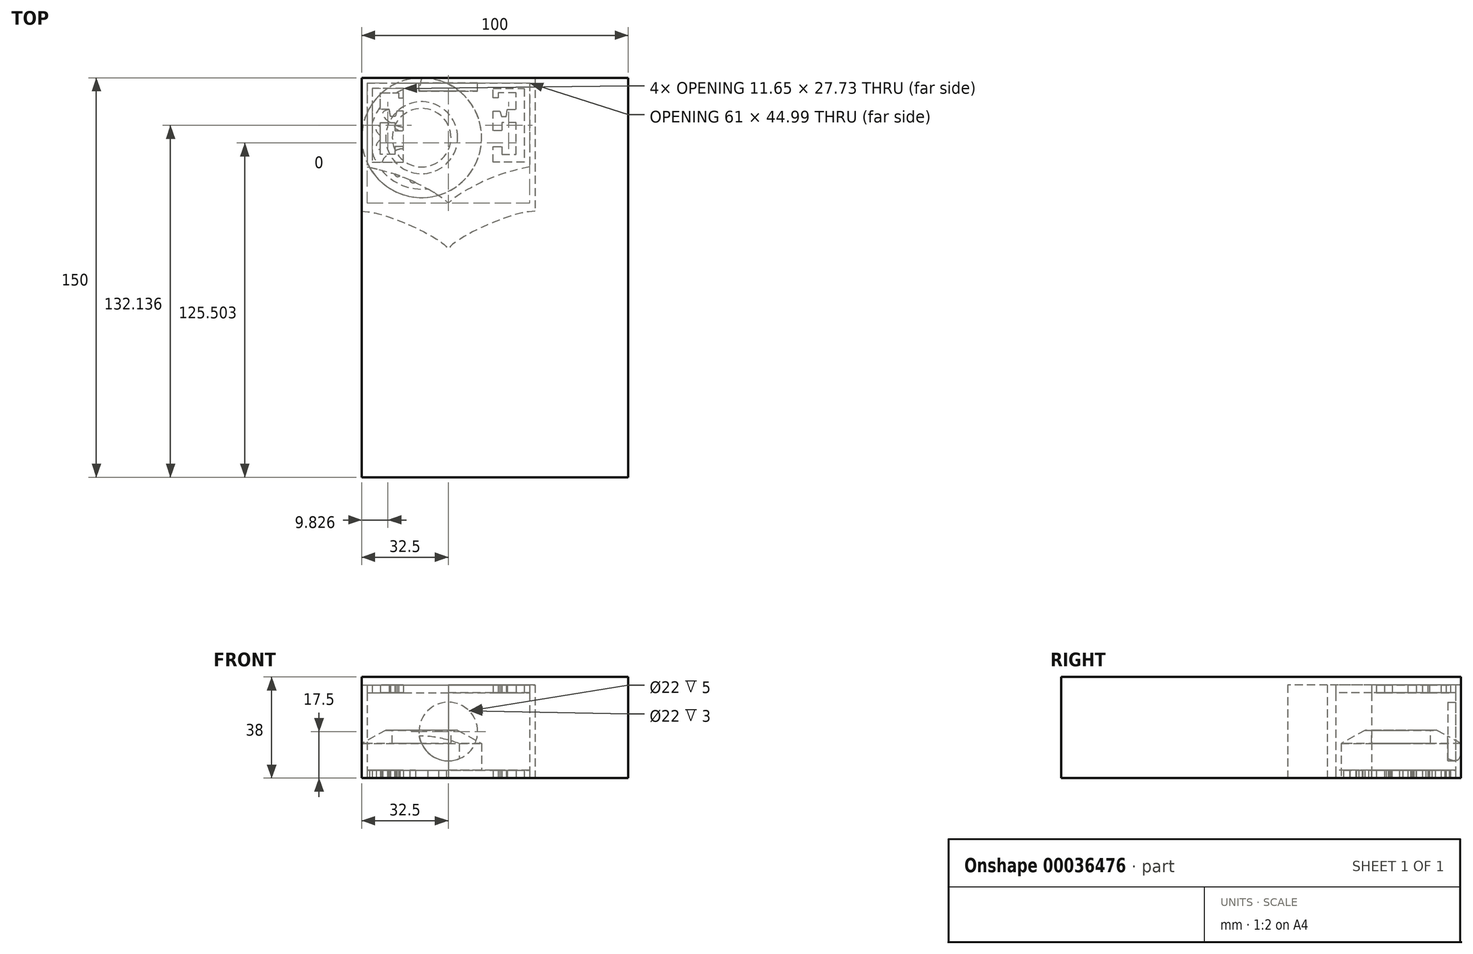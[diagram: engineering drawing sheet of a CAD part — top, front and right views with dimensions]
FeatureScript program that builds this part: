
annotation { "Feature Type Name" : "Feature", "Feature Type Description" : "" }
export const myFeature = defineFeature(function(context is Context, id is Id, definition is map)
    precondition{}
    {
        {
            var Q0;
            Q0=qCreatedBy(makeId("Top.planeOp"),FACE);
            var sketch = newSketch(context, id + "F0", { "sketchPlane" : qUnion([Q0])});
            skSolve(sketch);
        }
        {
            var Q0;
            Q0=qCreatedBy(makeId("Top.planeOp"),FACE);
            var sketch = newSketch(context, id + "F1", { "sketchPlane" : qUnion([Q0])});
            skLineSegment(sketch, "E0.0", {"start": v(0, 0) * mm, "end": v(0, -65) * mm, "construction": true});
            skLineSegment(sketch, "E1.0", {"start": v(65, 0) * mm, "end": v(0, 0) * mm, "construction": true});
            skLineSegment(sketch, "E2.0", {"start": v(0, -65) * mm, "end": v(65, -65) * mm, "construction": true});
            skLineSegment(sketch, "E3", {"start": v(32.5, 0) * mm, "end": v(32.5, -65) * mm, "construction": true});
            skLineSegment(sketch, "E4", {"start": v(32.5, 0) * mm, "end": v(0, 0) * mm});
            skLineSegment(sketch, "E5", {"start": v(0, 0) * mm, "end": v(0, -50.15) * mm});
            skFitSpline(sketch, "E6", {"points": [v(0, -50.15) * mm, v(3.66, -50.5) * mm, v(10.36, -52.32) * mm, v(21.46, -56.9) * mm, v(28.51, -60.84) * mm, v(31.27, -62.9) * mm, v(32.5, -65) * mm], "startDerivative": vector(25.8, -1.39) * mm, "endDerivative": vector(0, -17.33) * mm});
            skLineSegment(sketch, "E7.1", {"start": v(2, -2) * mm, "end": v(2, -33.52) * mm});
            skLineSegment(sketch, "E7.2", {"start": v(32.5, -2) * mm, "end": v(2, -2) * mm});
            skLineSegment(sketch, "E8", {"start": v(13.81, -7.5) * mm, "end": v(15.65, -7.5) * mm});
            skLineSegment(sketch, "E9", {"start": v(15.65, -7.5) * mm, "end": v(15.65, -4) * mm});
            skLineSegment(sketch, "E10", {"start": v(15.65, -4) * mm, "end": v(4, -4) * mm});
            skLineSegment(sketch, "E11", {"start": v(4, -4) * mm, "end": v(4, -31.73) * mm});
            skLineSegment(sketch, "E12", {"start": v(4, -31.73) * mm, "end": v(15.65, -31.73) * mm});
            skLineSegment(sketch, "E13", {"start": v(15.65, -31.73) * mm, "end": v(15.65, -25.83) * mm});
            skLineSegment(sketch, "E14", {"start": v(15.65, -25.83) * mm, "end": v(12.43, -25.83) * mm});
            skLineSegment(sketch, "E15", {"start": v(12.43, -25.83) * mm, "end": v(12.43, -28.7) * mm});
            skLineSegment(sketch, "E16", {"start": v(12.43, -28.7) * mm, "end": v(7.02, -28.7) * mm});
            skLineSegment(sketch, "E17", {"start": v(7.02, -28.7) * mm, "end": v(7.02, -16.77) * mm});
            skLineSegment(sketch, "E18", {"start": v(7.02, -16.77) * mm, "end": v(12.43, -16.77) * mm});
            skLineSegment(sketch, "E19", {"start": v(12.43, -16.77) * mm, "end": v(12.43, -19.9) * mm});
            skLineSegment(sketch, "E20", {"start": v(12.43, -19.9) * mm, "end": v(15.65, -19.9) * mm});
            skLineSegment(sketch, "E21", {"start": v(15.65, -19.9) * mm, "end": v(15.65, -12.5) * mm});
            skLineSegment(sketch, "E22", {"start": v(15.65, -12.5) * mm, "end": v(13.18, -12.5) * mm});
            skLineSegment(sketch, "E23", {"start": v(13.18, -12.5) * mm, "end": v(12.54, -14.54) * mm});
            skLineSegment(sketch, "E24", {"start": v(12.54, -14.54) * mm, "end": v(10.76, -14.54) * mm});
            skLineSegment(sketch, "E25", {"start": v(10.76, -14.54) * mm, "end": v(10.36, -11.89) * mm});
            skLineSegment(sketch, "E26", {"start": v(10.36, -11.89) * mm, "end": v(7.02, -11.89) * mm});
            skLineSegment(sketch, "E27", {"start": v(7.02, -11.89) * mm, "end": v(7.02, -5.62) * mm});
            skLineSegment(sketch, "E28", {"start": v(7.02, -5.62) * mm, "end": v(13.81, -5.62) * mm});
            skLineSegment(sketch, "E29", {"start": v(13.81, -5.62) * mm, "end": v(13.81, -7.5) * mm});
            skFitSpline(sketch, "E30", {"points": [v(32.5, -14.07) * mm, v(31.31, -16.82) * mm, v(29.03, -19.54) * mm, v(27.59, -20.35) * mm, v(25.23, -20.31) * mm, v(24.13, -19.17) * mm, v(24.1, -17.02) * mm, v(26.54, -15) * mm, v(26.34, -12.46) * mm, v(23.52, -11.92) * mm, v(21.24, -12.62) * mm, v(21.17, -14.07) * mm, v(21.2, -24.54) * mm, v(23.35, -27) * mm, v(26.61, -27.06) * mm, v(28.6, -27.9) * mm, v(30.64, -30.18) * mm, v(32.5, -32.97) * mm], "startDerivative": vector(-15.31, -45.36) * mm, "endDerivative": vector(28.23, -44.45) * mm});
            skLineSegment(sketch, "E31", {"start": v(32.5, -32.97) * mm, "end": v(32.5, -14.07) * mm});
            skLineSegment(sketch, "E32", {"start": v(32.5, -65) * mm, "end": v(32.5, -64.37) * mm});
            skLineSegment(sketch, "E33.MirrorCS", {"start": v(32.5, 0) * mm, "end": v(65, 0) * mm});
            skLineSegment(sketch, "E34.MirrorCS", {"start": v(32.5, -2) * mm, "end": v(63, -2) * mm});
            skLineSegment(sketch, "E35.MirrorCS", {"start": v(63, -2) * mm, "end": v(63, -33.52) * mm});
            skLineSegment(sketch, "E36.MirrorCS", {"start": v(65, 0) * mm, "end": v(65, -50.15) * mm});
            skFitSpline(sketch, "E37.MirrorCS", {"points": [v(65, -50.15) * mm, v(61.34, -50.5) * mm, v(54.64, -52.32) * mm, v(43.54, -56.9) * mm, v(36.49, -60.84) * mm, v(33.73, -62.9) * mm, v(32.5, -65) * mm], "startDerivative": vector(-25.8, -1.39) * mm, "endDerivative": vector(0, -17.33) * mm});
            skLineSegment(sketch, "E38.MirrorCS", {"start": v(49.35, -4) * mm, "end": v(61, -4) * mm});
            skLineSegment(sketch, "E39.MirrorCS", {"start": v(49.35, -7.5) * mm, "end": v(49.35, -4) * mm});
            skLineSegment(sketch, "E40.MirrorCS", {"start": v(57.98, -5.62) * mm, "end": v(51.19, -5.62) * mm});
            skLineSegment(sketch, "E41.MirrorCS", {"start": v(51.19, -5.62) * mm, "end": v(51.19, -7.5) * mm});
            skFitSpline(sketch, "E42.MirrorCS", {"points": [v(32.5, -14.07) * mm, v(33.69, -16.82) * mm, v(35.97, -19.54) * mm, v(37.41, -20.35) * mm, v(39.77, -20.31) * mm, v(40.87, -19.17) * mm, v(40.9, -17.02) * mm, v(38.46, -15) * mm, v(38.66, -12.46) * mm, v(41.48, -11.92) * mm, v(43.76, -12.62) * mm, v(43.83, -14.07) * mm, v(43.8, -24.54) * mm, v(41.65, -27) * mm, v(38.39, -27.06) * mm, v(36.4, -27.9) * mm, v(34.36, -30.18) * mm, v(32.5, -32.97) * mm], "startDerivative": vector(15.31, -45.36) * mm, "endDerivative": vector(-28.23, -44.45) * mm});
            skLineSegment(sketch, "E43.MirrorCS", {"start": v(49.35, -25.83) * mm, "end": v(52.57, -25.83) * mm});
            skLineSegment(sketch, "E44.MirrorCS", {"start": v(49.35, -31.73) * mm, "end": v(49.35, -25.83) * mm});
            skLineSegment(sketch, "E45.MirrorCS", {"start": v(52.57, -25.83) * mm, "end": v(52.57, -28.7) * mm});
            skLineSegment(sketch, "E46.MirrorCS", {"start": v(52.57, -28.7) * mm, "end": v(57.98, -28.7) * mm});
            skLineSegment(sketch, "E47.MirrorCS", {"start": v(61, -31.73) * mm, "end": v(49.35, -31.73) * mm});
            skLineSegment(sketch, "E48.MirrorCS", {"start": v(61, -4) * mm, "end": v(61, -31.73) * mm});
            skLineSegment(sketch, "E49.MirrorCS", {"start": v(57.98, -16.77) * mm, "end": v(52.57, -16.77) * mm});
            skLineSegment(sketch, "E50.MirrorCS", {"start": v(52.57, -16.77) * mm, "end": v(52.57, -19.9) * mm});
            skLineSegment(sketch, "E51.MirrorCS", {"start": v(52.57, -19.9) * mm, "end": v(49.35, -19.9) * mm});
            skLineSegment(sketch, "E52.MirrorCS", {"start": v(49.35, -19.9) * mm, "end": v(49.35, -12.5) * mm});
            skLineSegment(sketch, "E53.MirrorCS", {"start": v(49.35, -12.5) * mm, "end": v(51.82, -12.5) * mm});
            skLineSegment(sketch, "E54.MirrorCS", {"start": v(51.82, -12.5) * mm, "end": v(52.46, -14.54) * mm});
            skLineSegment(sketch, "E55.MirrorCS", {"start": v(52.46, -14.54) * mm, "end": v(54.24, -14.54) * mm});
            skLineSegment(sketch, "E56.MirrorCS", {"start": v(54.24, -14.54) * mm, "end": v(54.64, -11.89) * mm});
            skLineSegment(sketch, "E57.MirrorCS", {"start": v(54.64, -11.89) * mm, "end": v(57.98, -11.89) * mm});
            skLineSegment(sketch, "E58.MirrorCS", {"start": v(57.98, -11.89) * mm, "end": v(57.98, -5.62) * mm});
            skLineSegment(sketch, "E59.MirrorCS", {"start": v(51.19, -7.5) * mm, "end": v(49.35, -7.5) * mm});
            skLineSegment(sketch, "E60.MirrorCS", {"start": v(57.98, -28.7) * mm, "end": v(57.98, -16.77) * mm});
            skFitSpline(sketch, "E61", {"points": [v(2, -33.52) * mm, v(6.2, -34.35) * mm, v(11.5, -35.88) * mm, v(18.02, -38.31) * mm, v(23.08, -40.78) * mm, v(28.33, -43.78) * mm, v(32.5, -47) * mm], "startDerivative": vector(27.34, -4.07) * mm, "endDerivative": vector(26.33, -24.7) * mm});
            skLineSegment(sketch, "E62", {"start": v(32.5, -47) * mm, "end": v(32.5, -65) * mm});
            skFitSpline(sketch, "E63.MirrorCS", {"points": [v(63, -33.52) * mm, v(58.8, -34.35) * mm, v(53.5, -35.88) * mm, v(46.98, -38.31) * mm, v(41.92, -40.78) * mm, v(36.67, -43.78) * mm, v(32.5, -47) * mm], "startDerivative": vector(-27.34, -4.07) * mm, "endDerivative": vector(-26.33, -24.7) * mm});
            skSolve(sketch);
        }
        {
            var Q0;
            Q0=qCreatedBy(makeId("Top.planeOp"),FACE);
            var sketch = newSketch(context, id + "F2", { "sketchPlane" : qUnion([Q0])});
            skSolve(sketch);
        }
        {
            var Q0;
            Q0=qCreatedBy(makeId("Top.planeOp"),FACE);
            var sketch = newSketch(context, id + "F3", { "sketchPlane" : qUnion([Q0])});
            skLineSegment(sketch, "E64.0", {"start": v(0, 0) * mm, "end": v(0, -45) * mm, "construction": true});
            skLineSegment(sketch, "E65.0", {"start": v(45, 0) * mm, "end": v(0, 0) * mm, "construction": true});
            skCircle(sketch, "E66", {"center": v(22.5, -22.5) * mm, "radius": 22.5 * mm});
            skPoint(sketch, "E66.centerSnap0", {"position": v(0, -22.5) * mm});
            skPoint(sketch, "E66.centerSnap1", {"position": v(22.5, 0) * mm});
            skCircle(sketch, "E67", {"center": v(22.5, -22.5) * mm, "radius": 11.5 * mm});
            skSolve(sketch);
        }
        {
            var Q0;
            Q0=makeQuery(id+"F3.imprint","IMPRINT",FACE,{"disambiguationData":[TD([[makeQuery(id+"F3.imprint","IMPRINT",EDGE,{"derivedFrom":sQuery(id+"F3.wireOp",EDGE,"E66")}),1.0]])]});
            var Q1;
            Q1=makeQuery(id+"F3.imprint","IMPRINT",FACE,{"disambiguationData":[TD([[makeQuery(id+"F3.imprint","IMPRINT",EDGE,{"derivedFrom":sQuery(id+"F3.wireOp",EDGE,"E67")}),1.0]])]});
            extrude(context, id + "F4", {"entities" : qUnion([Q0, Q1]), "depth" : 18 * mm});
        }
        {
            var Q0;
            Q0=makeQuery(id+"F4.opExtrude","CAP_EDGE",EDGE,{"disambiguationData":[OSD([sQuery(id+"F3.wireOp",EDGE,"E66")])],"isStart":false});
            chamfer(context, id + "F5", {"entities" : qUnion([Q0]), "chamferType" : ChamferType.TWO_OFFSETS, "width1" : 9 * mm, "oppositeDirection" : false, "width2" : 5 * mm, "tangentPropagation" : true});
        }
        {
            var Q0;
            Q0=makeQuery(id+"F4.opExtrude","CAP_FACE",FACE,{"disambiguationData":[OSD([sQuery(id+"F3.wireOp",EDGE,"E66")])],"isStart":false});
            var sketch = newSketch(context, id + "F6", { "sketchPlane" : qUnion([Q0])});
            skCircle(sketch, "E68", {"center": v(22.5, -22.5) * mm, "radius": 11 * mm});
            skSolve(sketch);
        }
        {
            var Q0;
            Q0=makeQuery(id+"F6.imprint","IMPRINT",FACE,{"disambiguationData":[TD([[makeQuery(id+"F6.imprint","IMPRINT",EDGE,{"derivedFrom":sQuery(id+"F6.wireOp",EDGE,"E68")}),1.0]])]});
            extrude(context, id + "F7", {"entities" : qUnion([Q0]), "operationType" : NewBodyOperationType.REMOVE, "oppositeDirection" : true, "depth" : 5 * mm});
        }
        {
            var Q0;
            Q0=qCreatedBy(makeId("Top.planeOp"),FACE);
            var sketch = newSketch(context, id + "F8", { "sketchPlane" : qUnion([Q0])});
            skLineSegment(sketch, "E69.0", {"start": v(0, -45) * mm, "end": v(45, -45) * mm, "construction": true});
            skLineSegment(sketch, "E70.0", {"start": v(0, 0) * mm, "end": v(0, -45) * mm, "construction": true});
            skCircle(sketch, "E71", {"center": v(22.5, -22.5) * mm, "radius": 22.5 * mm});
            skPoint(sketch, "E71.centerSnap0", {"position": v(22.5, -45) * mm});
            skPoint(sketch, "E71.centerSnap1", {"position": v(0, -22.5) * mm});
            skCircle(sketch, "E72", {"center": v(22.5, -22.5) * mm, "radius": 19.33 * mm});
            skCircle(sketch, "E73", {"center": v(22.5, -22.5) * mm, "radius": 1.5 * mm});
            skCircle(sketch, "E74", {"center": v(22.5, -26.37) * mm, "radius": 1.34 * mm});
            skCircle(sketch, "E75.1.0", {"center": v(25.24, -25.24) * mm, "radius": 1.34 * mm});
            skCircle(sketch, "E75.2.0", {"center": v(26.37, -22.5) * mm, "radius": 1.34 * mm});
            skCircle(sketch, "E75.3.0", {"center": v(25.24, -19.76) * mm, "radius": 1.34 * mm});
            skCircle(sketch, "E75.4.0", {"center": v(22.5, -18.63) * mm, "radius": 1.34 * mm});
            skCircle(sketch, "E75.5.0", {"center": v(19.76, -19.76) * mm, "radius": 1.34 * mm});
            skCircle(sketch, "E75.6.0", {"center": v(18.63, -22.5) * mm, "radius": 1.34 * mm});
            skCircle(sketch, "E75.7.0", {"center": v(19.76, -25.24) * mm, "radius": 1.34 * mm});
            skLineSegment(sketch, "E76", {"start": v(22.5, -22.5) * mm, "end": v(20.04, -28.38) * mm, "construction": true});
            skLineSegment(sketch, "E77", {"start": v(22.5, -22.5) * mm, "end": v(29.44, -39.27) * mm, "construction": true});
            skLineSegment(sketch, "E78", {"start": v(22.5, -22.5) * mm, "end": v(22.5, -41.83) * mm, "construction": true});
            skFitSpline(sketch, "E79", {"points": [v(22.5, -37.34) * mm, v(25.27, -39.5) * mm, v(26.62, -39.04) * mm, v(26.85, -35.13) * mm, v(24.87, -30.63) * mm, v(23.82, -30.1) * mm, v(22.5, -31.1) * mm], "startDerivative": vector(14.86, -14.9) * mm, "endDerivative": vector(-10.08, -10.16) * mm});
            skFitSpline(sketch, "E80", {"points": [v(22.5, -39.95) * mm, v(23.6, -39.9) * mm, v(26.5, -40.44) * mm, v(27.67, -40.64) * mm, v(28.47, -40.37) * mm, v(29.14, -39.74) * mm, v(29.44, -39.27) * mm], "startDerivative": vector(11.19, 0.7) * mm, "endDerivative": vector(2.46, 3.4) * mm});
            skArc(sketch, "E81", {"start": v(20.04, -28.38) * mm, "mid": v(22.49, -28.88) * mm, "end": v(24.94, -28.4) * mm});
            skFitSpline(sketch, "E82.MirrorCS", {"points": [v(22.5, -37.34) * mm, v(19.73, -39.5) * mm, v(18.38, -39.04) * mm, v(18.15, -35.13) * mm, v(20.13, -30.63) * mm, v(21.18, -30.1) * mm, v(22.5, -31.1) * mm], "startDerivative": vector(-14.86, -14.9) * mm, "endDerivative": vector(10.08, -10.16) * mm});
            skFitSpline(sketch, "E83.MirrorCS", {"points": [v(22.5, -39.95) * mm, v(21.4, -39.9) * mm, v(18.5, -40.44) * mm, v(17.33, -40.64) * mm, v(16.53, -40.37) * mm, v(15.86, -39.74) * mm, v(15.56, -39.27) * mm], "startDerivative": vector(-11.19, 0.7) * mm, "endDerivative": vector(-2.46, 3.4) * mm});
            skLineSegment(sketch, "E84", {"start": v(29.9, -40.36) * mm, "end": v(24.94, -28.4) * mm});
            skLineSegment(sketch, "E85", {"start": v(20.04, -28.38) * mm, "end": v(15.11, -40.36) * mm});
            skCircle(sketch, "E86", {"center": v(22.5, -22.5) * mm, "radius": 6.38 * mm});
            skSolve(sketch);
        }
        {
            var Q0;
            Q0=makeQuery(id+"F8.imprint","IMPRINT",FACE,{"disambiguationData":[TD([[makeQuery(id+"F8.imprint","IMPRINT",EDGE,{"derivedFrom":sQuery(id+"F8.wireOp",EDGE,"E75.5.0")}),1.0]])]});
            var Q1;
            Q1=makeQuery(id+"F8.imprint","IMPRINT",FACE,{"disambiguationData":[TD([[makeQuery(id+"F8.imprint","IMPRINT",EDGE,{"derivedFrom":sQuery(id+"F8.wireOp",EDGE,"E75.6.0")}),1.0]])]});
            var Q2;
            Q2=makeQuery(id+"F8.imprint","IMPRINT",FACE,{"disambiguationData":[TD([[makeQuery(id+"F8.imprint","IMPRINT",EDGE,{"derivedFrom":sQuery(id+"F8.wireOp",EDGE,"E75.7.0")}),1.0]])]});
            var Q3;
            Q3=makeQuery(id+"F8.imprint","IMPRINT",FACE,{"disambiguationData":[TD([[makeQuery(id+"F8.imprint","IMPRINT",EDGE,{"derivedFrom":sQuery(id+"F8.wireOp",EDGE,"E74")}),1.0]])]});
            var Q4;
            Q4=makeQuery(id+"F8.imprint","IMPRINT",FACE,{"disambiguationData":[TD([[makeQuery(id+"F8.imprint","IMPRINT",EDGE,{"derivedFrom":sQuery(id+"F8.wireOp",EDGE,"E75.1.0")}),1.0]])]});
            var Q5;
            Q5=makeQuery(id+"F8.imprint","IMPRINT",FACE,{"disambiguationData":[TD([[makeQuery(id+"F8.imprint","IMPRINT",EDGE,{"derivedFrom":sQuery(id+"F8.wireOp",EDGE,"E75.2.0")}),1.0]])]});
            var Q6;
            Q6=makeQuery(id+"F8.imprint","IMPRINT",FACE,{"disambiguationData":[TD([[makeQuery(id+"F8.imprint","IMPRINT",EDGE,{"derivedFrom":sQuery(id+"F8.wireOp",EDGE,"E75.3.0")}),1.0]])]});
            var Q7;
            Q7=makeQuery(id+"F8.imprint","IMPRINT",FACE,{"disambiguationData":[TD([[makeQuery(id+"F8.imprint","IMPRINT",EDGE,{"derivedFrom":sQuery(id+"F8.wireOp",EDGE,"E75.4.0")}),1.0]])]});
            var Q8;
            Q8=makeQuery(id+"F8.imprint","IMPRINT",FACE,{"disambiguationData":[TD([[makeQuery(id+"F8.imprint","IMPRINT",EDGE,{"derivedFrom":sQuery(id+"F8.wireOp",EDGE,"E73")}),1.0]])]});
            var Q9;
            Q9=makeQuery(id+"F8.imprint","IMPRINT",FACE,{"disambiguationData":[TD([[makeQuery(id+"F8.imprint","IMPRINT",EDGE,{"derivedFrom":sQuery(id+"F8.wireOp",EDGE,"E72")}),1.0]])]});
            var Q10;
            Q10=makeQuery(id+"F8.imprint","IMPRINT",FACE,{"disambiguationData":[TD([[makeQuery(id+"F8.imprint","IMPRINT",EDGE,{"derivedFrom":sQuery(id+"F8.wireOp",EDGE,"E79")}),-1.0]])]});
            var Q11;
            Q11=makeQuery(id+"F8.imprint","IMPRINT",FACE,{"disambiguationData":[TD([[makeQuery(id+"F8.imprint","IMPRINT",EDGE,{"derivedFrom":sQuery(id+"F8.wireOp",EDGE,"E79")}),1.0]])]});
            var Q12;
            {var subQ3=sQuery(id+"F8.wireOp",EDGE,"E84");var subQ5=sQuery(id+"F8.wireOp",EDGE,"E72");var subQ9=makeQuery(id+"F8.imprint","INTERSECT",VERTEX,{"derivedFrom":[subQ5,subQ3]});Q12=makeQuery(id+"F8.imprint","IMPRINT",FACE,{"disambiguationData":[TD([[makeQuery(id+"F8.imprint","IMPRINT",EDGE,{"disambiguationData":[TD([[subQ9,-1.0]])],"derivedFrom":subQ5}),1.0]])]});}
            extrude(context, id + "F9", {"entities" : qUnion([Q0, Q1, Q2, Q3, Q4, Q5, Q6, Q7, Q8, Q9, Q10, Q11, Q12]), "operationType" : NewBodyOperationType.REMOVE, "depth" : 3 * mm});
        }
        {
            var Q0;
            Q0=makeQuery(id+"F8.imprint","IMPRINT",FACE,{"disambiguationData":[TD([[makeQuery(id+"F8.imprint","IMPRINT",EDGE,{"derivedFrom":sQuery(id+"F8.wireOp",EDGE,"E79")}),1.0]])]});
            extrude(context, id + "F10", {"entities" : qUnion([Q0]), "depth" : 3 * mm});
        }
        {
            var Q0;
            Q0=makeQuery(id+"F10.opExtrude","SWEPT_BODY",BODY,{"disambiguationData":[OSD([sQuery(id+"F8.wireOp",EDGE,"E79"),sQuery(id+"F8.wireOp",EDGE,"E82.MirrorCS")])]});
            var Q1;
            Q1=sQuery(id+"F8.wireOp",EDGE,"E73");
            circularPattern(context, id + "F11", {"entities" : qUnion([Q0]), "axis" : qUnion([Q1]), "angle" : 45 * degree, "instanceCount" : 8});
        }
        {
            var Q0;
            Q0 = qSketchRegion(id + "F1", true);
            var Q1;
            Q1=makeQuery(id+"F1.imprint","IMPRINT",FACE,{"disambiguationData":[TD([[makeQuery(id+"F1.imprint","IMPRINT",EDGE,{"derivedFrom":sQuery(id+"F1.wireOp",EDGE,"E7.1")}),1.0]])]});
            var Q2;
            Q2=makeQuery(id+"F1.imprint","IMPRINT",FACE,{"disambiguationData":[TD([[makeQuery(id+"F1.imprint","IMPRINT",EDGE,{"derivedFrom":sQuery(id+"F1.wireOp",EDGE,"E8")}),1.0]])]});
            var Q3;
            Q3=makeQuery(id+"F1.imprint","IMPRINT",FACE,{"disambiguationData":[TD([[makeQuery(id+"F1.imprint","IMPRINT",EDGE,{"derivedFrom":sQuery(id+"F1.wireOp",EDGE,"E30")}),1.0]])]});
            var Q4;
            Q4=makeQuery(id+"F1.imprint","IMPRINT",FACE,{"disambiguationData":[TD([[makeQuery(id+"F1.imprint","IMPRINT",EDGE,{"derivedFrom":sQuery(id+"F1.wireOp",EDGE,"E31")}),-1.0]])]});
            var Q5;
            Q5=makeQuery(id+"F1.imprint","IMPRINT",FACE,{"disambiguationData":[TD([[makeQuery(id+"F1.imprint","IMPRINT",EDGE,{"derivedFrom":sQuery(id+"F1.wireOp",EDGE,"E38.MirrorCS")}),-1.0]])]});
            extrude(context, id + "F12", {"entities" : qUnion([Q0, Q1, Q2, Q3, Q4, Q5]), "depth" : 35 * mm});
        }
        {
            var Q0;
            Q0=makeQuery(id+"F1.imprint","IMPRINT",FACE,{"disambiguationData":[TD([[makeQuery(id+"F1.imprint","IMPRINT",EDGE,{"derivedFrom":sQuery(id+"F1.wireOp",EDGE,"E7.1")}),1.0]])]});
            extrude(context, id + "F13", {"entities" : qUnion([Q0]), "operationType" : NewBodyOperationType.REMOVE, "depth" : 3 * mm});
        }
        {
            var Q0;
            Q0=makeQuery(id+"F1.imprint","IMPRINT",FACE,{"disambiguationData":[TD([[makeQuery(id+"F1.imprint","IMPRINT",EDGE,{"derivedFrom":sQuery(id+"F1.wireOp",EDGE,"E7.1")}),1.0]])]});
            var Q1;
            Q1=makeQuery(id+"F12.opExtrude","CAP_FACE",FACE,{"disambiguationData":[OSD([sQuery(id+"F1.wireOp",EDGE,"E4"),sQuery(id+"F1.wireOp",EDGE,"E5"),sQuery(id+"F1.wireOp",EDGE,"E6"),sQuery(id+"F1.wireOp",EDGE,"E33.MirrorCS"),sQuery(id+"F1.wireOp",EDGE,"E36.MirrorCS"),sQuery(id+"F1.wireOp",EDGE,"E37.MirrorCS")])],"isStart":false});
            extrude(context, id + "F14", {"entities" : qUnion([Q0]), "operationType" : NewBodyOperationType.REMOVE, "endBound" : BoundingType.UP_TO_SURFACE, "endBoundEntityFace" : qUnion([Q1]), "depth" : 34.25 * mm, "hasSecondDirection" : true, "secondDirectionOppositeDirection" : false, "secondDirectionDepth" : 32 * mm});
        }
        {
            var Q0;
            Q0=makeQuery(id+"F12.opExtrude","SWEPT_FACE",FACE,{"disambiguationData":[OSD([sQuery(id+"F1.wireOp",EDGE,"E4"),sQuery(id+"F1.wireOp",EDGE,"E33.MirrorCS")])]});
            var sketch = newSketch(context, id + "F15", { "sketchPlane" : qUnion([Q0])});
            skCircle(sketch, "E87", {"center": v(-32.5, 17.5) * mm, "radius": 11 * mm});
            skPoint(sketch, "E87.centerSnap0", {"position": v(-65, 17.5) * mm});
            skPoint(sketch, "E87.centerSnap1", {"position": v(-32.5, 0) * mm});
            skSolve(sketch);
        }
        {
            var Q0;
            Q0=makeQuery(id+"F15.imprint","IMPRINT",FACE,{"disambiguationData":[TD([[makeQuery(id+"F15.imprint","IMPRINT",EDGE,{"derivedFrom":sQuery(id+"F15.wireOp",EDGE,"E87")}),1.0]])]});
            extrude(context, id + "F16", {"entities" : qUnion([Q0]), "operationType" : NewBodyOperationType.REMOVE, "oppositeDirection" : true, "depth" : 5 * mm});
        }
        {
            var Q0;
            Q0=qCreatedBy(makeId("Top.planeOp"),FACE);
            var sketch = newSketch(context, id + "F17", { "sketchPlane" : qUnion([Q0])});
            skLineSegment(sketch, "E88.bottom", {"start": v(0, 0) * mm, "end": v(100, 0) * mm});
            skLineSegment(sketch, "E88.top", {"start": v(0, -150) * mm, "end": v(100, -150) * mm});
            skLineSegment(sketch, "E88.left", {"start": v(0, 0) * mm, "end": v(0, -150) * mm});
            skLineSegment(sketch, "E88.right", {"start": v(100, 0) * mm, "end": v(100, -150) * mm});
            skSolve(sketch);
        }
        {
            var Q0;
            Q0=makeQuery(id+"F17.imprint","IMPRINT",FACE,{"disambiguationData":[TD([[makeQuery(id+"F17.imprint","IMPRINT",EDGE,{"derivedFrom":sQuery(id+"F17.wireOp",EDGE,"E88.bottom")}),-1.0]])]});
            extrude(context, id + "F18", {"entities" : qUnion([Q0]), "depth" : 38 * mm});
        }
        {
            var Q0;
            Q0=qCreatedBy(makeId("Top.planeOp"),FACE);
            cPlane(context, id + "F19", {"entities" : qUnion([Q0]), "cplaneType" : CPlaneType.OFFSET, "offset" : 10 * mm, "width" : 150 * mm, "height" : 150 * mm});
        }
        {
            var Q0;
            Q0=qCreatedBy(id+"F19.planeOp",FACE);
            cPlane(context, id + "F20", {"entities" : qUnion([Q0]), "cplaneType" : CPlaneType.OFFSET, "offset" : 5 * mm, "width" : 150 * mm, "height" : 150 * mm});
        }
    });
